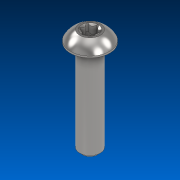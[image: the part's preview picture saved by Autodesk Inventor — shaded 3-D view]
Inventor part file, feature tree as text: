
AUTODESK INVENTOR PART (.ipt)
format: ipt  version: 2022.2 (Build 262287000, 287)  size: 179,200 bytes
history: native  units: in
note: dims shown in document units (in); Inventor stores cm internally (conversion verified against a paired STEP export)
features: direct_edit x1, chamfer x1, move_body x1
ambient origin geometry x8: Origin, YZ Plane, XZ Plane, XY Plane, X Axis, Y Axis, Z Axis, Center Point
bodies: Solid1 (feature_tree)
feature tree (3):
  direct_edit  "Direct Edit1"
  chamfer  "Chamfer2"  [1 undecoded]
  move_body  "Move1"
note: 1 required parameter value undecoded (feature->parameter linkage not recoverable at this tier; creation-order binding heuristic only, values carry confidence <= 0.55)
